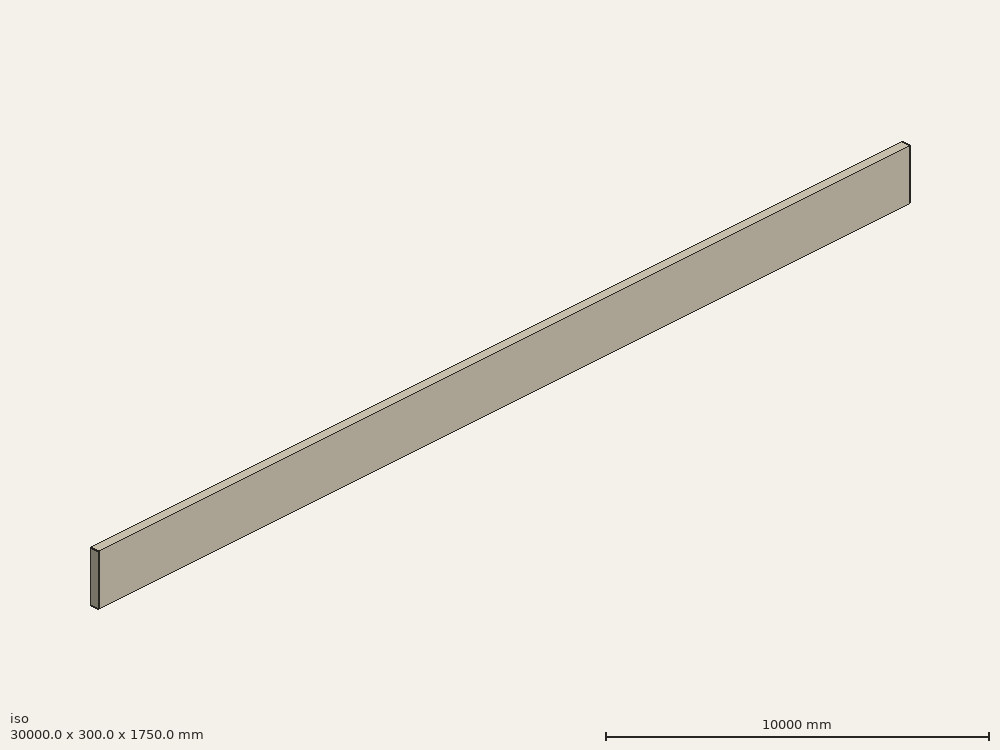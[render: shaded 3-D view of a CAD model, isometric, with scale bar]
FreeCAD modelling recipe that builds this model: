
FCSTD DOCUMENT  (FreeCAD 0.21R33694 (Git))
Label: box girder
License: All rights reserved
LicenseURL: http://en.wikipedia.org/wiki/All_rights_reserved
objects: Sketcher::SketchObject×3, Part::Face×3, Part::Extrusion×3, Fem::ConstraintDisplacement×2, Fem::ConstraintForce×2, Part::FeaturePython×1, Fem::FemMeshObjectPython×1, Fem::FemSolverObjectPython×1, App::MaterialObjectPython×1, Fem::FemAnalysis×1
note: 10 computed .brp shape members not serialized (recipe doc carries the construction recipe); baked Part::Feature solids carry a one-line shape summary decoded from their .brp

FEATURE [Sketcher::SketchObject] Sketch
  FullyConstrained = true
  Placement = pos=(0,0,0) rot=(0.57735,0.57735,0.57735;2.0944rad)
  sketch-geometry (8):
    g0: LineSegment StartX=0 StartY=0 StartZ=0 EndX=300 EndY=0 EndZ=0
    g1: LineSegment StartX=300 StartY=0 StartZ=0 EndX=300 EndY=1750 EndZ=0
    g2: LineSegment StartX=300 StartY=1750 StartZ=0 EndX=0 EndY=1750 EndZ=0
    g3: LineSegment StartX=0 StartY=1750 StartZ=0 EndX=0 EndY=0 EndZ=0
    g4: LineSegment StartX=10 StartY=1740 StartZ=0 EndX=290 EndY=1740 EndZ=0
    g5: LineSegment StartX=290 StartY=1740 StartZ=0 EndX=290 EndY=10 EndZ=0
    g6: LineSegment StartX=290 StartY=10 StartZ=0 EndX=10 EndY=10 EndZ=0
    g7: LineSegment StartX=10 StartY=10 StartZ=0 EndX=10 EndY=1740 EndZ=0
  constraints (23):
    c: Coincident(g0,g1)
    c: Coincident(g1,g2)
    c: Coincident(g2,g3)
    c: Coincident(g3,g0)
    c: Horizontal(g0)
    c: Horizontal(g2)
    c: Vertical(g1)
    c: Vertical(g3)
    c: Coincident(g0,g-1)
    c: DistanceY(g1,g1) = 1750
    c: DistanceX(g0,g0) = 300
    c: Coincident(g4,g5)
    c: Coincident(g5,g6)
    c: Coincident(g6,g7)
    c: Coincident(g7,g4)
    c: Horizontal(g4)
    c: Horizontal(g6)
    c: Vertical(g5)
    c: Vertical(g7)
    c: DistanceY(g0,g6) = 10
    c: DistanceX(g0,g6) = 10
    c: DistanceX(g6,g6) = 280
    c: DistanceY(g7,g7) = 1730
FEATURE [Part::Face] Face
  FaceMakerClass = Part::FaceMakerBullseye
  Sources = -> [Sketch]
FEATURE [Part::Extrusion] Extrude  label="box"
  Base = -> Face
  Dir = (1,0,0)
  DirMode = 2
  FaceMakerClass = Part::FaceMakerBullseye
  LengthFwd = 30000
  LengthRev = 0
  Solid = false
  Symmetric = false
FEATURE [Sketcher::SketchObject] Sketch001
  FullyConstrained = true
  Placement = pos=(0,0,0) rot=(0.57735,0.57735,0.57735;2.0944rad)
  sketch-geometry (4):
    g0: LineSegment StartX=0 StartY=0 StartZ=0 EndX=300 EndY=0 EndZ=0
    g1: LineSegment StartX=300 StartY=0 StartZ=0 EndX=300 EndY=1750 EndZ=0
    g2: LineSegment StartX=300 StartY=1750 StartZ=0 EndX=0 EndY=1750 EndZ=0
    g3: LineSegment StartX=0 StartY=1750 StartZ=0 EndX=0 EndY=0 EndZ=0
  constraints (11):
    c: Coincident(g0,g1)
    c: Coincident(g1,g2)
    c: Coincident(g2,g3)
    c: Coincident(g3,g0)
    c: Horizontal(g0)
    c: Horizontal(g2)
    c: Vertical(g1)
    c: Vertical(g3)
    c: Coincident(g0,g-1)
    c: DistanceY(g1,g1) = 1750
    c: DistanceX(g0,g0) = 300
FEATURE [Part::Face] Face001
  FaceMakerClass = Part::FaceMakerBullseye
  Sources = -> [Sketch001]
FEATURE [Part::Extrusion] Extrude001  label="end plate 1"
  Base = -> Face001
  Dir = (1,0,0)
  DirMode = 2
  FaceMakerClass = Part::FaceMakerBullseye
  LengthFwd = 25
  LengthRev = 0
  Solid = false
  Symmetric = false
FEATURE [Sketcher::SketchObject] Sketch002
  FullyConstrained = true
  Placement = pos=(0,0,0) rot=(0.57735,0.57735,0.57735;2.0944rad)
  sketch-geometry (4):
    g0: LineSegment StartX=0 StartY=0 StartZ=0 EndX=300 EndY=0 EndZ=0
    g1: LineSegment StartX=300 StartY=0 StartZ=0 EndX=300 EndY=1750 EndZ=0
    g2: LineSegment StartX=300 StartY=1750 StartZ=0 EndX=0 EndY=1750 EndZ=0
    g3: LineSegment StartX=0 StartY=1750 StartZ=0 EndX=0 EndY=0 EndZ=0
  constraints (11):
    c: Coincident(g0,g1)
    c: Coincident(g1,g2)
    c: Coincident(g2,g3)
    c: Coincident(g3,g0)
    c: Horizontal(g0)
    c: Horizontal(g2)
    c: Vertical(g1)
    c: Vertical(g3)
    c: Coincident(g0,g-1)
    c: DistanceY(g1,g1) = 1750
    c: DistanceX(g0,g0) = 300
FEATURE [Part::Face] Face002
  FaceMakerClass = Part::FaceMakerBullseye
  Sources = -> [Sketch002]
FEATURE [Part::Extrusion] Extrude002  label="end plate 2"
  Base = -> Face002
  Dir = (1,0,0)
  DirMode = 2
  FaceMakerClass = Part::FaceMakerBullseye
  LengthFwd = 25
  LengthRev = 0
  Placement = pos=(29975,0,0) rot=(0,0,1;0rad)
  Solid = false
  Symmetric = false
FEATURE [Fem::ConstraintDisplacement] ConstraintDisplacement
  NormalDirection = (0,0,1)
  Normals = (4) [(0,0,1),(0,0,1),(0,0,1),(0,0,1)]
  Points = (4) [(30000,0,0),(30000,100,0),(30000,200,0),(30000,300,0)]
  References = -> [Extrude]
  Scale = 19
  hasXFormula = false
  hasYFormula = false
  hasZFormula = false
  rotxFix = false
  rotxFree = true
  rotyFix = false
  rotyFree = true
  rotzFix = false
  rotzFree = true
  useFlowSurfaceForce = false
  xDisplacement = 0
  xFix = false
  xFree = true
  xRotation = 0
  yDisplacement = 0
  yFix = false
  yFree = false
  yRotation = 0
  zDisplacement = 0
  zFix = false
  zFree = false
  zRotation = 0
FEATURE [Fem::ConstraintDisplacement] ConstraintDisplacement001
  NormalDirection = (0,0,1)
  Normals = (4) [(0,0,1),(0,0,1),(0,0,1),(0,0,1)]
  Points = (4) [(0,0,0),(0,100,0),(0,200,0),(0,300,0)]
  References = -> [Sketch]
  Scale = 19
  hasXFormula = false
  hasYFormula = false
  hasZFormula = false
  rotxFix = false
  rotxFree = true
  rotyFix = false
  rotyFree = true
  rotzFix = false
  rotzFree = true
  useFlowSurfaceForce = false
  xDisplacement = 0
  xFix = false
  xFree = false
  xRotation = 0
  yDisplacement = 0
  yFix = false
  yFree = false
  yRotation = 0
  zDisplacement = 0
  zFix = false
  zFree = false
  zRotation = 0
FEATURE [Part::FeaturePython] BooleanFragments  # WARN: FeaturePython — macro-defined, semantics opaque (R4)
  Mode = 2
  Objects = -> [Extrude,Extrude001,Extrude002]
  Tolerance = 0
FEATURE [Fem::ConstraintForce] ConstraintForce
  DirectionVector = (0,0,-1)
  Force = 900000
  NormalDirection = (0,0,1)
  Points = (140) [(29975,300,1750),(29975,200,1750),(29975,100,1750),(29975,0,1750),(29094.1,300,1750),(29094.1,200,1750),(29094.1,100,1750),(29094.1,0,1750),+132 more]
  References = -> [BooleanFragments]
  Reversed = true
  Scale = 89
FEATURE [Fem::FemMeshObjectPython] FEMMeshGmsh  # FEM object (typed FeaturePython)
  Algorithm2D = 0
  Algorithm3D = 0
  CharacteristicLengthMax = 300
  CharacteristicLengthMin = 0
  CoherenceMesh = true
  ElementDimension = 0
  ElementOrder = 1
  GeometryTolerance = 1e-06
  GroupsOfNodes = false
  HighOrderOptimize = 0
  MeshSizeFromCurvature = 12
  OptimizeNetgen = false
  OptimizeStd = true
  Part = -> BooleanFragments
  RecombinationAlgorithm = 0
  Recombine3DAll = false
  RecombineAll = false
  SecondOrderLinear = false
FEATURE [Fem::FemSolverObjectPython] SolverCcxTools  # FEM object (typed FeaturePython)
  AnalysisType = 0
  BeamShellResultOutput3D = false
  BucklingFactors = 1
  EigenmodeHighLimit = 1000000
  EigenmodeLowLimit = 0
  EigenmodesCount = 10
  GeometricalNonlinearity = 0
  IterationsControlParameterCutb = 0.25,0.5,0.75,0.85,,,1.5,
  IterationsControlParameterIter = 4,8,9,200,10,400,,200,,
  IterationsControlParameterTimeUse = false
  IterationsThermoMechMaximum = 2000
  IterationsUserDefinedIncrementations = false
  IterationsUserDefinedTimeStepLength = false
  MaterialNonlinearity = 0
  MatrixSolverType = 0
  SplitInputWriter = false
  ThermoMechSteadyState = true
  TimeEnd = 1
  TimeInitialStep = 0.01
FEATURE [App::MaterialObjectPython] MaterialSolid  # material (typed FeaturePython)
  Category = 0
  Material = AuthorAndLicense=(c) 2014 M. Münch - GNU Lesser General Public License (LGPL),CardName=Steel-St-E-315,Density=7800 kg/m^3,Father=Metal,+13 more (map truncated)
FEATURE [Fem::ConstraintForce] ConstraintForce001
  DirectionVector = (0,0,1)
  Force = 996893
  NormalDirection = (0,0,-1)
  Points = (32) [(25,0,0),(25,100,0),(25,200,0),(25,300,0),(16.6667,0,0),(16.6667,100,0),(16.6667,200,0),(16.6667,300,0),(8.33333,0,0),(8.33333,100,0),(8.33333,200,0),+21 more]
  References = -> [BooleanFragments]
  Reversed = true
  Scale = 13
FEATURE [Fem::FemAnalysis] Analysis
  Group = -> [ConstraintDisplacement,ConstraintDisplacement001,ConstraintForce,FEMMeshGmsh,SolverCcxTools,MaterialSolid,ConstraintForce001]
